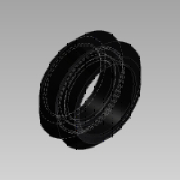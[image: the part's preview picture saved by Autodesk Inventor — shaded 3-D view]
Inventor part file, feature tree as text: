
AUTODESK INVENTOR PART (.ipt)
format: ipt  version: 2013 SP2 (Build 170200200, 200)  size: 151,040 bytes
history: native  units: mm
features: revolve x1, sketch x1
ambient origin geometry x8: Origin, YZ Plane, XZ Plane, XY Plane, X Axis, Y Axis, Z Axis, Center Point
bodies: Solid1 (feature_tree)
feature tree (2):
  revolve  "Revolution1"  [1 undecoded]
  sketch  "Sketch1"  dims[d0=10.0mm d2=0.5mm d3=15.974mm d4=13.89mm d5=0.3mm d6=0.3mm d7=19.54mm d8=5.12mm d12=24.39mm d14=18.75mm d16=0.275mm d17=135.0deg d18=135.0deg d19=2.695mm d20=90.0deg]
note: 1 required parameter value undecoded (feature->parameter linkage not recoverable at this tier; creation-order binding heuristic only, values carry confidence <= 0.55)
